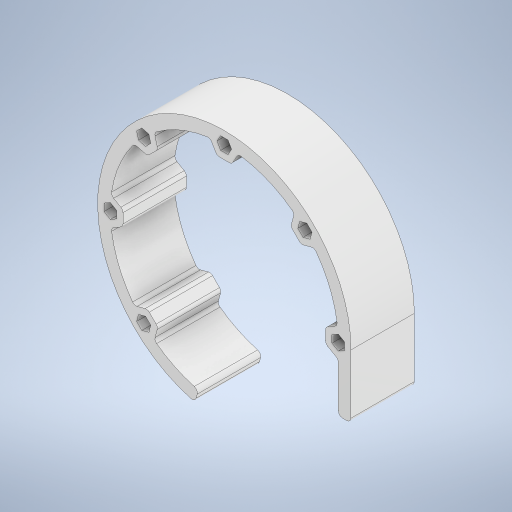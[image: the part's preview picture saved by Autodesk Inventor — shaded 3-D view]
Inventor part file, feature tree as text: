
AUTODESK INVENTOR PART (.ipt)
format: ipt  version: 2024.3 (Build 283343000, 343)  size: 1,064,448 bytes
history: native  units: mm
features: sketch x10, extrude x7, fillet x6, hole x3, other x1, projected_geometry x1
ambient origin geometry x8: Origin, YZ Plane, XZ Plane, XY Plane, X Axis, Y Axis, Z Axis, Center Point
bodies: Body1 (feature_tree)
feature tree (28):
  other  "ソリッド1"
  extrude  "押し出し1"  Depth=120.0mm
  hole  "穴1"  [1 undecoded]
  extrude  "押し出し3"  Depth=92.0mm
  extrude  "押し出し10"  TaperAngle=22.5deg  [1 undecoded]
  hole  "穴8"  [1 undecoded]
  fillet  "フィレット4"  Radius=60.0mm
  hole  "穴13"  [1 undecoded]
  fillet  "フィレット11"  Radius=210.0mm
  extrude  "押し出し17"  Depth=210.0mm
  extrude  "押し出し18"  Depth=3.0mm TaperAngle=0.0deg
  fillet  "フィレット15"  [1 undecoded]
  fillet  "フィレット16"  Radius=14.835299mm
  fillet  "フィレット17"  Radius=14.835299mm
  extrude  "押し出し19"  Depth=60.0mm
  extrude  "押し出し20"  Depth=10.0mm TaperAngle=0.0deg
  fillet  "フィレット18"  Radius=180.0mm
  sketch  "スケッチ1"
  sketch  "スケッチ2"
  sketch  "スケッチ4"
  sketch  "スケッチ17"
  sketch  "スケッチ20"
  sketch  "スケッチ28"
  sketch  "スケッチ32"
  sketch  "スケッチ33"
  sketch  "スケッチ34"
  sketch  "スケッチ35"
  projected_geometry  "投影ループ2"
note: 5 required parameter values undecoded (feature->parameter linkage not recoverable at this tier; creation-order binding heuristic only, values carry confidence <= 0.55)
